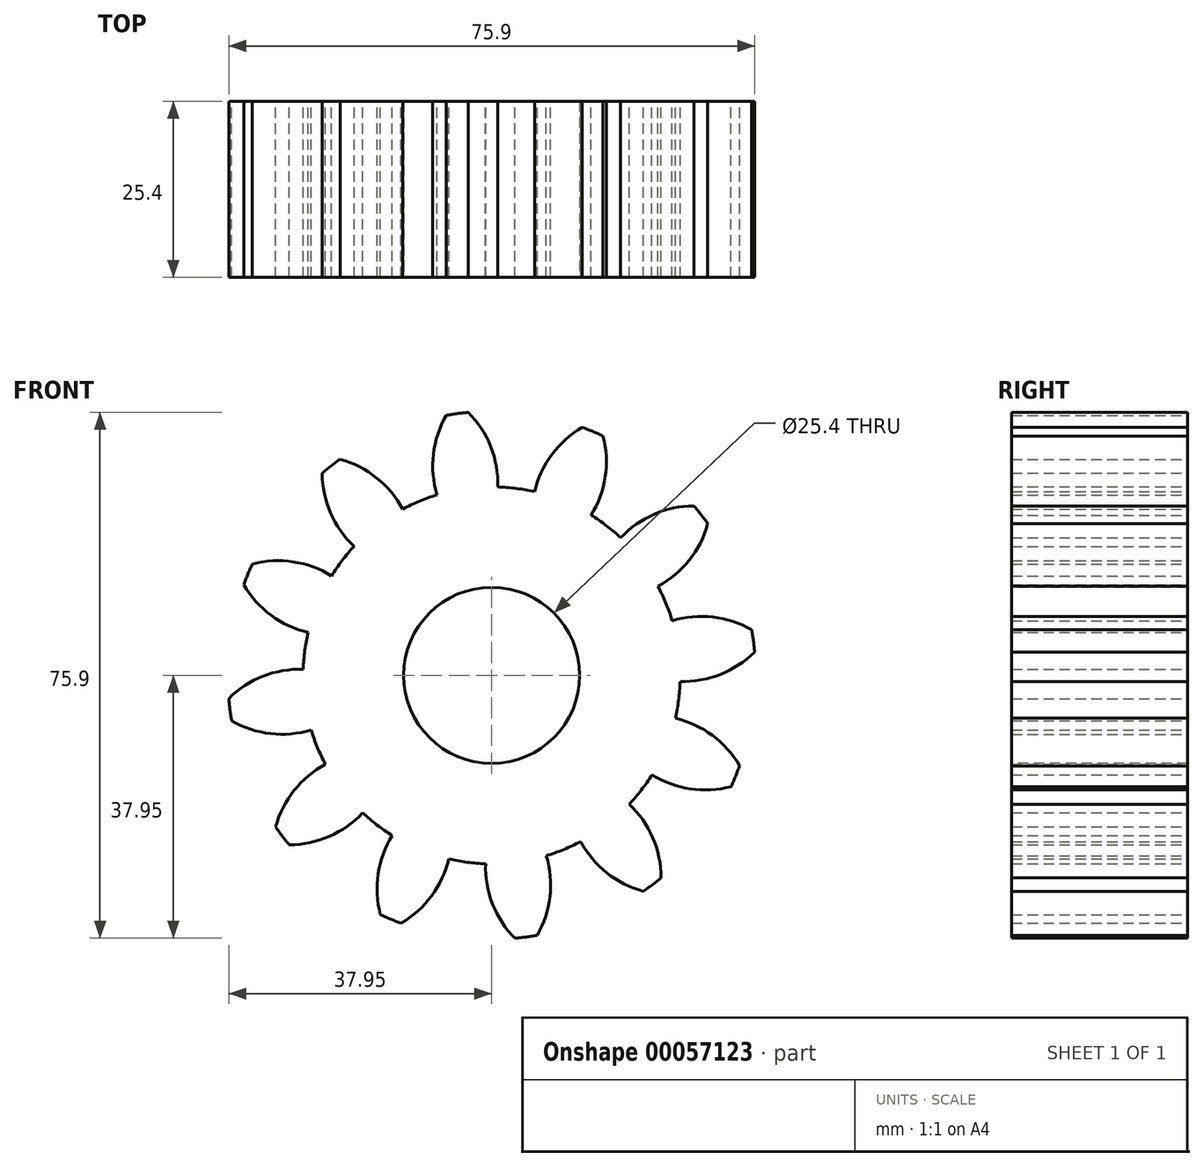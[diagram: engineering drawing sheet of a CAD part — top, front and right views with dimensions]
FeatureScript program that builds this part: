
annotation { "Feature Type Name" : "Feature", "Feature Type Description" : "" }
export const myFeature = defineFeature(function(context is Context, id is Id, definition is map)
    precondition{}
    {
        {
            assignVariable(context, id + "F0", {"name" : "NOT", "anyValue" : 12});
        }
        {
            var Q0;
            Q0=qCreatedBy(makeId("Front.planeOp"),FACE);
            var sketch = newSketch(context, id + "F1", { "sketchPlane" : qUnion([Q0])});
            skCircle(sketch, "E0", {"center": v(0, 0) * mm, "radius": 38.1 * mm});
            skCircle(sketch, "E1", {"center": v(0, 0) * mm, "radius": 32.66 * mm});
            skCircle(sketch, "E2", {"center": v(0, 0) * mm, "radius": 27.21 * mm});
            skLineSegment(sketch, "E3", {"start": v(0, 0) * mm, "end": v(0, 56.5) * mm});
            skLineSegment(sketch, "E4", {"start": v(0, 0) * mm, "end": v(-7.42, 56.35) * mm});
            skLineSegment(sketch, "E5", {"start": v(0, 32.66) * mm, "end": v(-56.68, 32.66) * mm});
            skLineSegment(sketch, "E6", {"start": v(0, 32.66) * mm, "end": v(-52.94, 13.39) * mm});
            skCircle(sketch, "E7", {"center": v(0, 32.66) * mm, "radius": 14.6 * mm});
            skArc(sketch, "E8", {"start": v(0.87, 27.2) * mm, "mid": v(-0.13, 33.01) * mm, "end": v(-3.36, 37.95) * mm});
            skArc(sketch, "E9.MirrorCS", {"start": v(-7.88, 26.05) * mm, "mid": v(-8.41, 31.92) * mm, "end": v(-6.58, 37.53) * mm});
            skSolve(sketch);
        }
        {
            var Q0;
            {var subQ0=sQuery(id+"F1.wireOp",EDGE,"E3");var subQ1=sQuery(id+"F1.wireOp",EDGE,"E2");var subQ2=makeQuery(id+"F1.imprint","INTERSECT",VERTEX,{"derivedFrom":[subQ1,subQ0]});Q0=makeQuery(id+"F1.imprint","IMPRINT",FACE,{"disambiguationData":[TD([[makeQuery(id+"F1.imprint","IMPRINT",EDGE,{"disambiguationData":[TD([[subQ2,-1.0]])],"derivedFrom":subQ1}),-1.0]])]});}
            var Q1;
            {var subQ0=sQuery(id+"F1.wireOp",EDGE,"E9.MirrorCS");var subQ1=sQuery(id+"F1.wireOp",EDGE,"E2");var subQ2=makeQuery(id+"F1.imprint","INTERSECT",VERTEX,{"derivedFrom":[subQ1,subQ0]});Q1=makeQuery(id+"F1.imprint","IMPRINT",FACE,{"disambiguationData":[TD([[makeQuery(id+"F1.imprint","IMPRINT",EDGE,{"disambiguationData":[TD([[subQ2,1.0]])],"derivedFrom":subQ1}),-1.0]])]});}
            var Q2;
            {var subQ0=sQuery(id+"F1.wireOp",EDGE,"E4");var subQ1=sQuery(id+"F1.wireOp",EDGE,"E1");var subQ2=makeQuery(id+"F1.imprint","INTERSECT",VERTEX,{"derivedFrom":[subQ1,subQ0]});Q2=makeQuery(id+"F1.imprint","IMPRINT",FACE,{"disambiguationData":[TD([[makeQuery(id+"F1.imprint","IMPRINT",EDGE,{"disambiguationData":[TD([[subQ2,-1.0]])],"derivedFrom":subQ1}),1.0]])]});}
            var Q3;
            {var subQ0=sQuery(id+"F1.wireOp",EDGE,"E4");var subQ1=sQuery(id+"F1.wireOp",EDGE,"E1");var subQ2=makeQuery(id+"F1.imprint","INTERSECT",VERTEX,{"derivedFrom":[subQ1,subQ0]});Q3=makeQuery(id+"F1.imprint","IMPRINT",FACE,{"disambiguationData":[TD([[makeQuery(id+"F1.imprint","IMPRINT",EDGE,{"disambiguationData":[TD([[subQ2,-1.0]])],"derivedFrom":subQ1}),-1.0]])]});}
            var Q4;
            {var subQ1=sQuery(id+"F1.wireOp",EDGE,"E1");var subQ3=sQuery(id+"F1.wireOp",EDGE,"E4");var subQ4=makeQuery(id+"F1.imprint","INTERSECT",VERTEX,{"derivedFrom":[subQ1,subQ3]});Q4=makeQuery(id+"F1.imprint","IMPRINT",FACE,{"disambiguationData":[TD([[makeQuery(id+"F1.imprint","IMPRINT",EDGE,{"disambiguationData":[TD([[subQ4,1.0]])],"derivedFrom":subQ3}),-1.0]])]});}
            var Q5;
            {var subQ1=sQuery(id+"F1.wireOp",EDGE,"E1");var subQ3=sQuery(id+"F1.wireOp",EDGE,"E4");var subQ4=makeQuery(id+"F1.imprint","INTERSECT",VERTEX,{"derivedFrom":[subQ1,subQ3]});Q5=makeQuery(id+"F1.imprint","IMPRINT",FACE,{"disambiguationData":[TD([[makeQuery(id+"F1.imprint","IMPRINT",EDGE,{"disambiguationData":[TD([[subQ4,-1.0]])],"derivedFrom":subQ3}),-1.0]])]});}
            var Q6;
            {var subQ0=sQuery(id+"F1.wireOp",EDGE,"E8");var subQ1=sQuery(id+"F1.wireOp",EDGE,"E0");var subQ2=makeQuery(id+"F1.imprint","INTERSECT",VERTEX,{"derivedFrom":[subQ1,subQ0]});Q6=makeQuery(id+"F1.imprint","IMPRINT",FACE,{"disambiguationData":[TD([[makeQuery(id+"F1.imprint","IMPRINT",EDGE,{"disambiguationData":[TD([[subQ2,-1.0]])],"derivedFrom":subQ1}),1.0]])]});}
            var Q7;
            {var subQ0=sQuery(id+"F1.wireOp",EDGE,"E9.MirrorCS");var subQ1=sQuery(id+"F1.wireOp",EDGE,"E0");var subQ2=makeQuery(id+"F1.imprint","INTERSECT",VERTEX,{"derivedFrom":[subQ1,subQ0]});Q7=makeQuery(id+"F1.imprint","IMPRINT",FACE,{"disambiguationData":[TD([[makeQuery(id+"F1.imprint","IMPRINT",EDGE,{"disambiguationData":[TD([[subQ2,1.0]])],"derivedFrom":subQ1}),1.0]])]});}
            var Q8;
            {var subQ0=sQuery(id+"F1.wireOp",EDGE,"E8");var subQ1=sQuery(id+"F1.wireOp",EDGE,"E2");var subQ2=makeQuery(id+"F1.imprint","INTERSECT",VERTEX,{"derivedFrom":[subQ1,subQ0]});Q8=makeQuery(id+"F1.imprint","IMPRINT",FACE,{"disambiguationData":[TD([[makeQuery(id+"F1.imprint","IMPRINT",EDGE,{"disambiguationData":[TD([[subQ2,-1.0]])],"derivedFrom":subQ1}),-1.0]])]});}
            var Q9;
            {var subQ0=sQuery(id+"F1.wireOp",EDGE,"E7");var subQ1=sQuery(id+"F1.wireOp",EDGE,"E2");var subQ8=makeQuery(id+"F1.imprint","INTERSECT",VERTEX,{"disambiguationData":[OD(0.0)],"derivedFrom":[subQ1,subQ0]});Q9=makeQuery(id+"F1.imprint","IMPRINT",FACE,{"disambiguationData":[TD([[makeQuery(id+"F1.imprint","IMPRINT",EDGE,{"disambiguationData":[TD([[subQ8,1.0]])],"derivedFrom":subQ1}),1.0]])]});}
            var Q10;
            {var subQ0=sQuery(id+"F1.wireOp",EDGE,"E2");var subQ1=makeQuery(id+"F1.imprint","INTERSECT",VERTEX,{"derivedFrom":[subQ0,sQuery(id+"F1.wireOp",EDGE,"E9.MirrorCS")]});Q10=makeQuery(id+"F1.imprint","IMPRINT",FACE,{"disambiguationData":[TD([[makeQuery(id+"F1.imprint","IMPRINT",EDGE,{"disambiguationData":[TD([[subQ1,1.0]])],"derivedFrom":subQ0}),1.0]])]});}
            var Q11;
            {var subQ0=sQuery(id+"F1.wireOp",EDGE,"E3");var subQ1=sQuery(id+"F1.wireOp",EDGE,"E2");var subQ2=makeQuery(id+"F1.imprint","INTERSECT",VERTEX,{"derivedFrom":[subQ1,subQ0]});Q11=makeQuery(id+"F1.imprint","IMPRINT",FACE,{"disambiguationData":[TD([[makeQuery(id+"F1.imprint","IMPRINT",EDGE,{"disambiguationData":[TD([[subQ2,-1.0]])],"derivedFrom":subQ1}),1.0]])]});}
            var Q12;
            {var subQ0=sQuery(id+"F1.wireOp",EDGE,"E4");var subQ1=sQuery(id+"F1.wireOp",EDGE,"E3");var subQ2=makeQuery(id+"F1.imprint","INTERSECT",VERTEX,{"derivedFrom":[subQ1,subQ0]});Q12=makeQuery(id+"F1.imprint","IMPRINT",FACE,{"disambiguationData":[TD([[makeQuery(id+"F1.imprint","IMPRINT",EDGE,{"disambiguationData":[TD([[subQ2,-1.0]])],"derivedFrom":subQ1}),1.0]])]});}
            var Q13;
            {var subQ0=sQuery(id+"F1.wireOp",EDGE,"E2");var subQ1=makeQuery(id+"F1.imprint","INTERSECT",VERTEX,{"derivedFrom":[subQ0,sQuery(id+"F1.wireOp",EDGE,"E8")]});Q13=makeQuery(id+"F1.imprint","IMPRINT",FACE,{"disambiguationData":[TD([[makeQuery(id+"F1.imprint","IMPRINT",EDGE,{"disambiguationData":[TD([[subQ1,1.0]])],"derivedFrom":subQ0}),1.0]])]});}
            extrude(context, id + "F2", {"entities" : qUnion([Q0, Q1, Q2, Q3, Q4, Q5, Q6, Q7, Q8, Q9, Q10, Q11, Q12, Q13]), "depth" : 25.4 * mm, "symmetric" : true});
        }
        {
            var Q0;
            Q0=makeQuery(id+"F2.opExtrude","SWEPT_BODY",BODY,{"disambiguationData":[OSD([sQuery(id+"F1.wireOp",EDGE,"E0"),sQuery(id+"F1.wireOp",EDGE,"E2"),sQuery(id+"F1.wireOp",EDGE,"E8"),sQuery(id+"F1.wireOp",EDGE,"E9.MirrorCS")])]});
            var Q1;
            Q1=makeQuery(id+"F2.opExtrude","SWEPT_FACE",FACE,{"disambiguationData":[OSD([sQuery(id+"F1.wireOp",EDGE,"E2")])]});
            circularPattern(context, id + "F3", {"operationType" : NewBodyOperationType.ADD, "entities" : qUnion([Q0]), "axis" : qUnion([Q1]), "angle" : (360 / getVariable(context, 'NOT')) * degree, "instanceCount" : getVariable(context, 'NOT')});
        }
        {
            var Q0;
            {var subQ0=makeQuery(id+"F2.opExtrude","CAP_FACE",FACE,{"disambiguationData":[OSD([sQuery(id+"F1.wireOp",EDGE,"E0"),sQuery(id+"F1.wireOp",EDGE,"E2"),sQuery(id+"F1.wireOp",EDGE,"E8"),sQuery(id+"F1.wireOp",EDGE,"E9.MirrorCS")])],"isStart":false});Q0=makeQuery(id+"F3.boolean.opBoolean","MERGE",FACE,{"derivedFrom":[subQ0,makeQuery(id+"F3.opPattern","COPY",FACE,{"derivedFrom":subQ0,"instanceName":"1"}),makeQuery(id+"F3.opPattern","COPY",FACE,{"derivedFrom":subQ0,"instanceName":"2"}),makeQuery(id+"F3.opPattern","COPY",FACE,{"derivedFrom":subQ0,"instanceName":"3"}),makeQuery(id+"F3.opPattern","COPY",FACE,{"derivedFrom":subQ0,"instanceName":"4"}),makeQuery(id+"F3.opPattern","COPY",FACE,{"derivedFrom":subQ0,"instanceName":"5"}),makeQuery(id+"F3.opPattern","COPY",FACE,{"derivedFrom":subQ0,"instanceName":"6"}),makeQuery(id+"F3.opPattern","COPY",FACE,{"derivedFrom":subQ0,"instanceName":"7"}),makeQuery(id+"F3.opPattern","COPY",FACE,{"derivedFrom":subQ0,"instanceName":"8"}),makeQuery(id+"F3.opPattern","COPY",FACE,{"derivedFrom":subQ0,"instanceName":"9"}),makeQuery(id+"F3.opPattern","COPY",FACE,{"derivedFrom":subQ0,"instanceName":"10"}),makeQuery(id+"F3.opPattern","COPY",FACE,{"derivedFrom":subQ0,"instanceName":"11"})]});}
            var sketch = newSketch(context, id + "F4", { "sketchPlane" : qUnion([Q0])});
            skPoint(sketch, "E10", {"position": v(0, 0) * mm});
            skSolve(sketch);
        }
        {
            var Q0;
            Q0=sQuery(id+"F4.wireOp",VERTEX,"E10");
            var Q1;
            Q1=makeQuery(id+"F2.opExtrude","SWEPT_BODY",BODY,{"disambiguationData":[OSD([sQuery(id+"F1.wireOp",EDGE,"E0"),sQuery(id+"F1.wireOp",EDGE,"E2"),sQuery(id+"F1.wireOp",EDGE,"E8"),sQuery(id+"F1.wireOp",EDGE,"E9.MirrorCS")])]});
            hole(context, id + "F5", {"style" : HoleStyle.SIMPLE, "holeDiameter" : 25.4 * mm, "endStyle" : HoleEndStyle.THROUGH, "locations" : qUnion([Q0]), "scope" : qUnion([Q1])});
        }
    });
